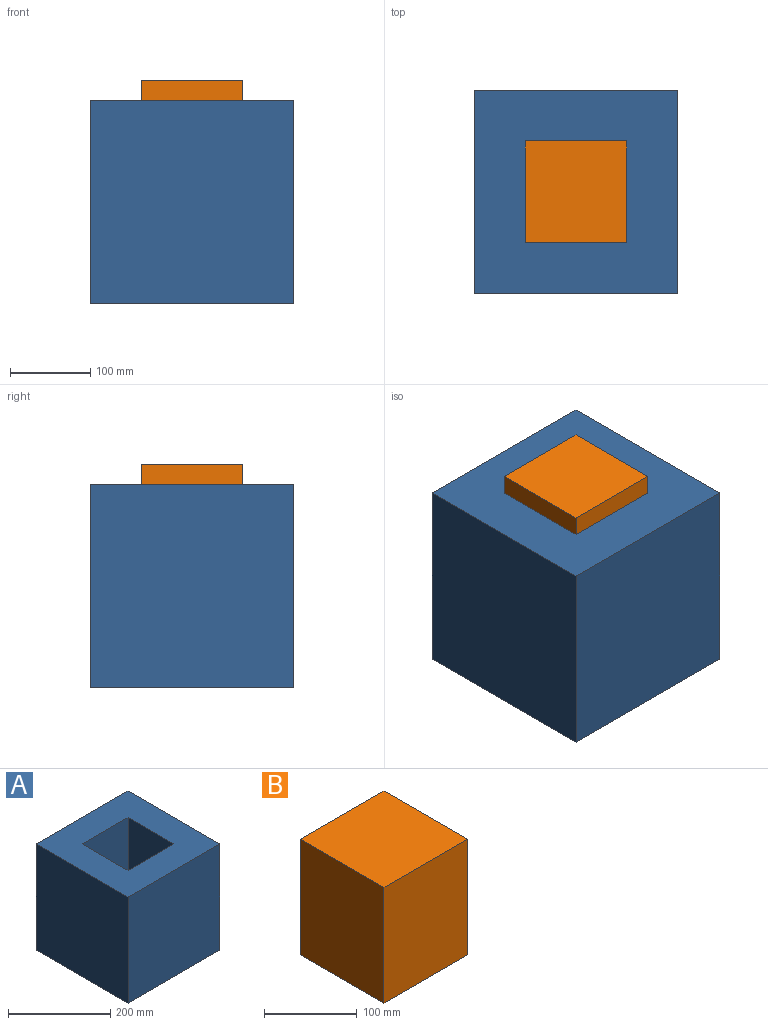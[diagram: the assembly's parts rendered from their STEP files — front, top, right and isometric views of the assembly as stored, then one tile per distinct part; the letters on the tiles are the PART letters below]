
ASSEMBLY  parts=2 mates=1
PART A: 11 faces, bbox 254x254x254 mm
  f0: plane 254x254mm, normal (0,0,1), area 48387mm2, adj f1,f2,f3,f4,f6,f7,f8,f9
  f1: plane 254x254mm, normal (0,1,0), area 64516mm2, adj f0,f2,f4,f5
  f2: plane 254x254mm, normal (-1,0,0), area 64516mm2, adj f0,f1,f3,f5
  f3: plane 254x254mm, normal (0,-1,0), area 64516mm2, adj f0,f2,f4,f5
  f4: plane 254x254mm, normal (1,0,0), area 64516mm2, adj f0,f1,f3,f5
  f5: plane 254x254mm, normal (0,0,-1), area 64516mm2, adj f1,f2,f3,f4
  f6: plane 127x127mm, normal (0,1,0), area 16129mm2, adj f0,f7,f9,f10
  f7: plane 127x127mm, normal (-1,0,0), area 16129mm2, adj f0,f6,f8,f10
  f8: plane 127x127mm, normal (0,-1,0), area 16129mm2, adj f0,f7,f9,f10
  f9: plane 127x127mm, normal (1,0,0), area 16129mm2, adj f0,f6,f8,f10
  f10: plane 127x127mm, normal (0,0,1), area 16129mm2, adj f6,f7,f8,f9
PART B: 6 faces, bbox 127x127x152.4 mm
  f0: plane 152.4x127mm, normal (0,-1,0), area 19354.8mm2, adj f1,f3,f4,f5
  f1: plane 152.4x127mm, normal (1,0,0), area 19354.8mm2, adj f0,f2,f4,f5
  f2: plane 152.4x127mm, normal (0,1,0), area 19354.8mm2, adj f1,f3,f4,f5
  f3: plane 152.4x127mm, normal (-1,0,0), area 19354.8mm2, adj f0,f2,f4,f5
  f4: plane 127x127mm, normal (0,0,1), area 16129mm2, adj f0,f1,f2,f3
  f5: plane 127x127mm, normal (0,0,-1), area 16129mm2, adj f0,f1,f2,f3
PLACE A at identity fixed
PLACE B rot(axis=(0,1,0),180deg) t=(127,127,279.4)mm
MATE fastened A.f10 <-> B.f4  axis (0,0,1) through (127,127,127)mm
